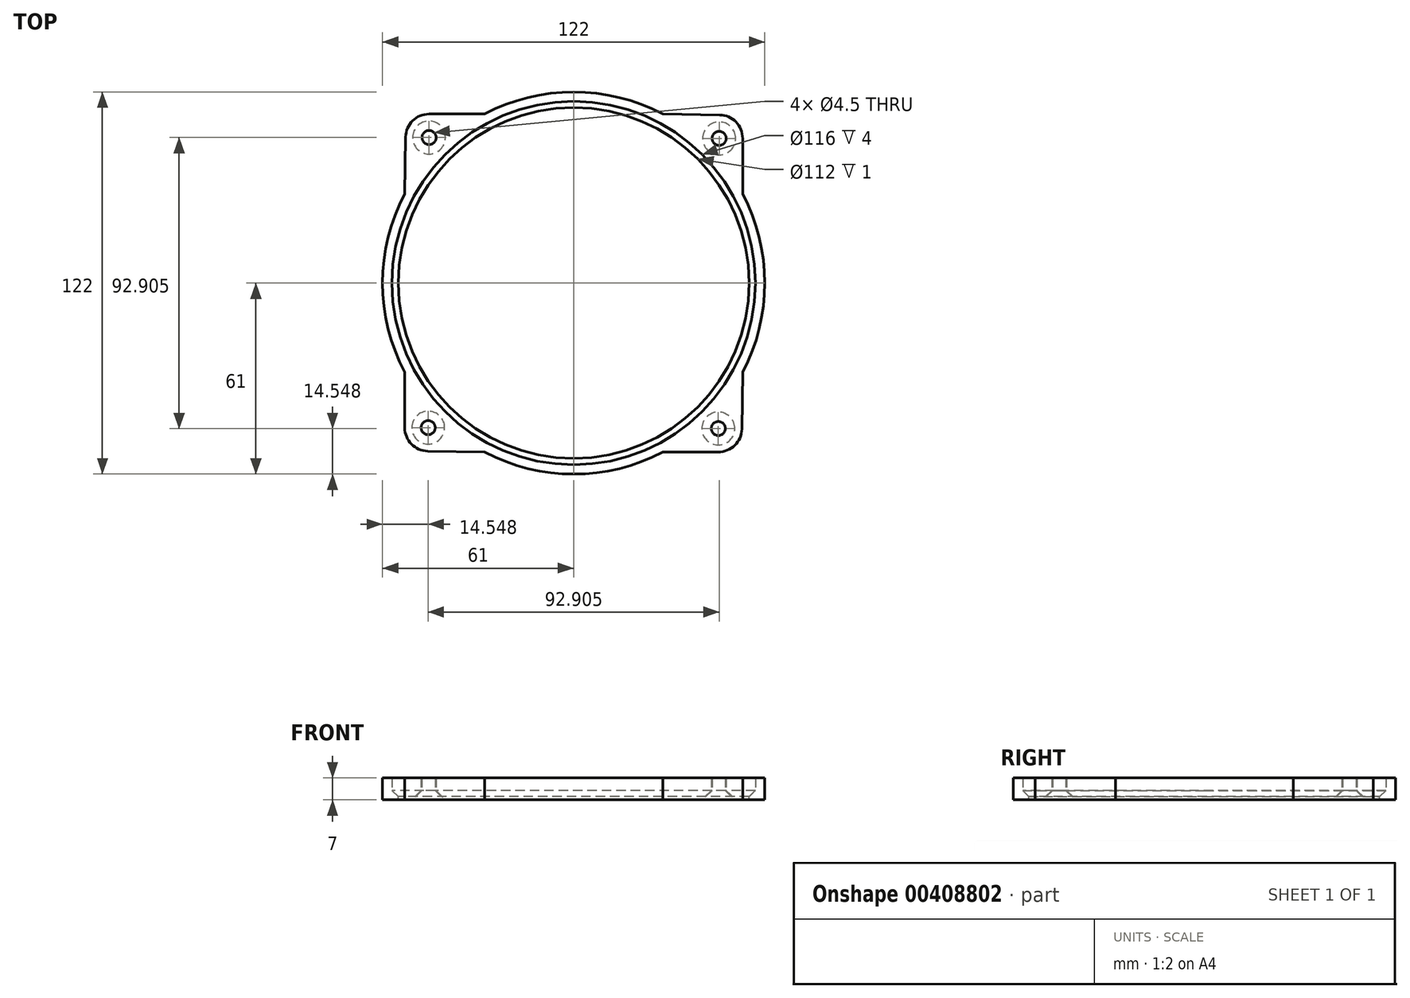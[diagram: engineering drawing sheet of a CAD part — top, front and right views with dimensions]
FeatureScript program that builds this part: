
annotation { "Feature Type Name" : "Feature", "Feature Type Description" : "" }
export const myFeature = defineFeature(function(context is Context, id is Id, definition is map)
    precondition{}
    {
        {
            var Q0;
            Q0=qCreatedBy(makeId("Top.planeOp"),FACE);
            var sketch = newSketch(context, id + "F0", { "sketchPlane" : qUnion([Q0])});
            skCircle(sketch, "E0", {"center": v(0, 0) * mm, "radius": 58 * mm});
            skCircle(sketch, "E1", {"center": v(0, 0) * mm, "radius": 61 * mm});
            skSolve(sketch);
        }
        {
            var Q0;
            Q0=makeQuery(id+"F0.imprint","IMPRINT",FACE,{"disambiguationData":[TD([[makeQuery(id+"F0.imprint","IMPRINT",EDGE,{"derivedFrom":sQuery(id+"F0.wireOp",EDGE,"E0")}),-1.0]])]});
            extrude(context, id + "F1", {"entities" : qUnion([Q0]), "depth" : 4 * mm});
        }
        {
            var Q0;
            Q0=qCreatedBy(makeId("Top.planeOp"),FACE);
            var sketch = newSketch(context, id + "F2", { "sketchPlane" : qUnion([Q0])});
            skCircle(sketch, "E2.0", {"center": v(0, 0) * mm, "radius": 56 * mm});
            skCircle(sketch, "E3.0", {"center": v(0, 0) * mm, "radius": 61 * mm});
            skSolve(sketch);
        }
        {
            var Q0;
            Q0=makeQuery(id+"F2.imprint","IMPRINT",FACE,{"disambiguationData":[TD([[makeQuery(id+"F2.imprint","IMPRINT",EDGE,{"derivedFrom":sQuery(id+"F2.wireOp",EDGE,"E2.0")}),-1.0]])]});
            extrude(context, id + "F3", {"entities" : qUnion([Q0]), "operationType" : NewBodyOperationType.ADD, "oppositeDirection" : true, "depth" : 3 * mm});
        }
        {
            var Q0;
            Q0=makeQuery(id+"F3.opExtrude","CAP_EDGE",EDGE,{"disambiguationData":[OSD([sQuery(id+"F2.wireOp",EDGE,"E2.0")])],"isStart":true});
            chamfer(context, id + "F4", {"entities" : qUnion([Q0]), "width" : 2 * mm, "tangentPropagation" : true});
        }
        {
            var Q0;
            Q0=makeQuery(id+"F3.opExtrude","CAP_FACE",FACE,{"disambiguationData":[OSD([sQuery(id+"F2.wireOp",EDGE,"E2.0"),sQuery(id+"F2.wireOp",EDGE,"E3.0")])],"isStart":false});
            var sketch = newSketch(context, id + "F5", { "sketchPlane" : qUnion([Q0])});
            skCircle(sketch, "E4", {"center": v(-46.45, 46.18) * mm, "radius": 7.5 * mm});
            skLineSegment(sketch, "E5", {"start": v(-53.95, 46.18) * mm, "end": v(-53.95, 28.46) * mm});
            skCircle(sketch, "E6", {"center": v(-46.45, 46.18) * mm, "radius": 2.25 * mm});
            skLineSegment(sketch, "E7", {"start": v(-46.57, 53.68) * mm, "end": v(-28.43, 53.97) * mm});
            skLineSegment(sketch, "E8.1.0", {"start": v(-53.68, -46.57) * mm, "end": v(-53.97, -28.43) * mm});
            skCircle(sketch, "E8.1.1", {"center": v(-46.18, -46.45) * mm, "radius": 7.5 * mm});
            skCircle(sketch, "E8.1.2", {"center": v(-46.18, -46.45) * mm, "radius": 2.25 * mm});
            skLineSegment(sketch, "E8.1.3", {"start": v(-46.18, -53.95) * mm, "end": v(-28.46, -53.95) * mm});
            skLineSegment(sketch, "E8.2.0", {"start": v(46.57, -53.68) * mm, "end": v(28.43, -53.97) * mm});
            skCircle(sketch, "E8.2.1", {"center": v(46.45, -46.18) * mm, "radius": 7.5 * mm});
            skCircle(sketch, "E8.2.2", {"center": v(46.45, -46.18) * mm, "radius": 2.25 * mm});
            skLineSegment(sketch, "E8.2.3", {"start": v(53.95, -46.18) * mm, "end": v(53.95, -28.46) * mm});
            skLineSegment(sketch, "E8.3.0", {"start": v(53.68, 46.57) * mm, "end": v(53.97, 28.43) * mm});
            skCircle(sketch, "E8.3.1", {"center": v(46.18, 46.45) * mm, "radius": 7.5 * mm});
            skCircle(sketch, "E8.3.2", {"center": v(46.18, 46.45) * mm, "radius": 2.25 * mm});
            skLineSegment(sketch, "E8.3.3", {"start": v(46.18, 53.95) * mm, "end": v(28.46, 53.95) * mm});
            skPoint(sketch, "E8.center", {"position": v(0, 0) * mm});
            skSolve(sketch);
        }
        {
            var Q0;
            Q0 = qSketchRegion(id + "F5", true);
            var Q1;
            {var subQ0=sQuery(id+"F5.wireOp",EDGE,"E5");Q1=makeQuery(id+"F5.imprint","IMPRINT",FACE,{"disambiguationData":[TD([[makeQuery(id+"F5.imprint","IMPRINT",EDGE,{"derivedFrom":subQ0}),1.0]])]});}
            var Q2;
            {var subQ0=sQuery(id+"F5.wireOp",EDGE,"E7");Q2=makeQuery(id+"F5.imprint","IMPRINT",FACE,{"disambiguationData":[TD([[makeQuery(id+"F5.imprint","IMPRINT",EDGE,{"derivedFrom":subQ0}),-1.0]])]});}
            var Q3;
            {var subQ0=sQuery(id+"F5.wireOp",EDGE,"E8.3.3");Q3=makeQuery(id+"F5.imprint","IMPRINT",FACE,{"disambiguationData":[TD([[makeQuery(id+"F5.imprint","IMPRINT",EDGE,{"derivedFrom":subQ0}),1.0]])]});}
            var Q4;
            {var subQ0=sQuery(id+"F5.wireOp",EDGE,"E8.3.0");Q4=makeQuery(id+"F5.imprint","IMPRINT",FACE,{"disambiguationData":[TD([[makeQuery(id+"F5.imprint","IMPRINT",EDGE,{"derivedFrom":subQ0}),-1.0]])]});}
            var Q5;
            {var subQ0=sQuery(id+"F5.wireOp",EDGE,"E8.2.3");Q5=makeQuery(id+"F5.imprint","IMPRINT",FACE,{"disambiguationData":[TD([[makeQuery(id+"F5.imprint","IMPRINT",EDGE,{"derivedFrom":subQ0}),1.0]])]});}
            var Q6;
            {var subQ0=sQuery(id+"F5.wireOp",EDGE,"E8.2.0");Q6=makeQuery(id+"F5.imprint","IMPRINT",FACE,{"disambiguationData":[TD([[makeQuery(id+"F5.imprint","IMPRINT",EDGE,{"derivedFrom":subQ0}),-1.0]])]});}
            var Q7;
            {var subQ0=sQuery(id+"F5.wireOp",EDGE,"E8.1.3");Q7=makeQuery(id+"F5.imprint","IMPRINT",FACE,{"disambiguationData":[TD([[makeQuery(id+"F5.imprint","IMPRINT",EDGE,{"derivedFrom":subQ0}),1.0]])]});}
            var Q8;
            {var subQ0=sQuery(id+"F5.wireOp",EDGE,"E8.1.0");Q8=makeQuery(id+"F5.imprint","IMPRINT",FACE,{"disambiguationData":[TD([[makeQuery(id+"F5.imprint","IMPRINT",EDGE,{"derivedFrom":subQ0}),-1.0]])]});}
            extrude(context, id + "F6", {"entities" : qUnion([Q0, Q1, Q2, Q3, Q4, Q5, Q6, Q7, Q8]), "operationType" : NewBodyOperationType.ADD, "oppositeDirection" : true, "depth" : 7 * mm});
        }
        {
            var Q0;
            Q0=makeQuery(id+"F6.opExtrude","CAP_EDGE",EDGE,{"disambiguationData":[OSD([sQuery(id+"F5.wireOp",EDGE,"E8.3.2")])],"isStart":true});
            var Q1;
            Q1=makeQuery(id+"F6.opExtrude","CAP_EDGE",EDGE,{"disambiguationData":[OSD([sQuery(id+"F5.wireOp",EDGE,"E8.2.2")])],"isStart":true});
            var Q2;
            Q2=makeQuery(id+"F6.opExtrude","CAP_EDGE",EDGE,{"disambiguationData":[OSD([sQuery(id+"F5.wireOp",EDGE,"E8.1.2")])],"isStart":true});
            var Q3;
            Q3=makeQuery(id+"F6.opExtrude","CAP_EDGE",EDGE,{"disambiguationData":[OSD([sQuery(id+"F5.wireOp",EDGE,"E6")])],"isStart":true});
            chamfer(context, id + "F7", {"entities" : qUnion([Q0, Q1, Q2, Q3]), "width" : 3 * mm, "tangentPropagation" : true});
        }
    });
